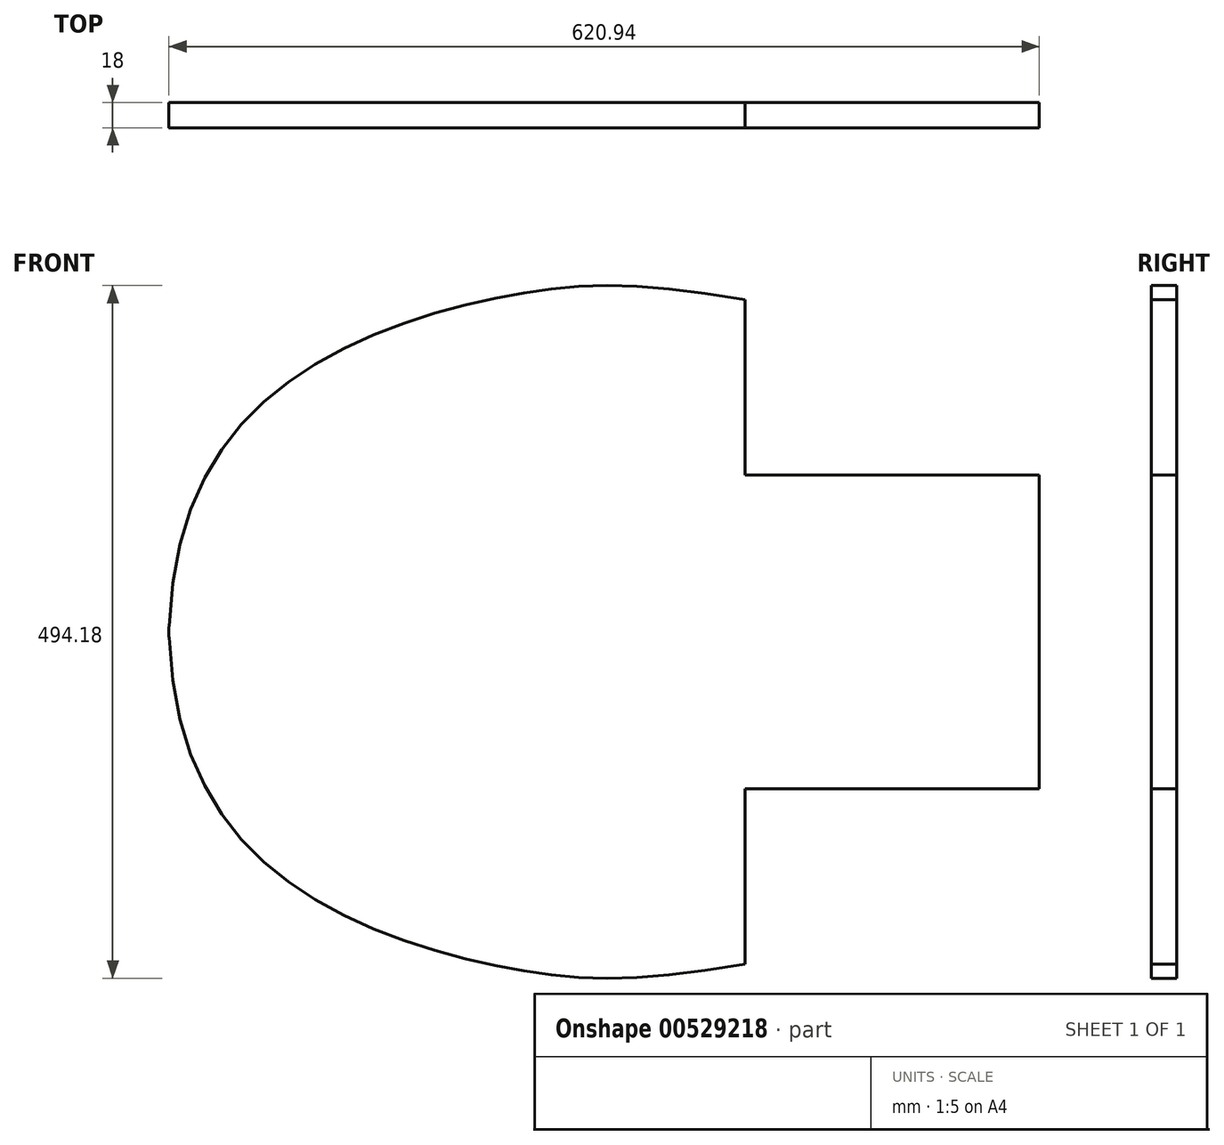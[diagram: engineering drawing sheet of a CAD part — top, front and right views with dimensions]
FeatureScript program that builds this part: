
annotation { "Feature Type Name" : "Feature", "Feature Type Description" : "" }
export const myFeature = defineFeature(function(context is Context, id is Id, definition is map)
    precondition{}
    {
        {
            var Q0;
            Q0=qCreatedBy(makeId("Front.planeOp"),FACE);
            var sketch = newSketch(context, id + "F0", { "sketchPlane" : qUnion([Q0])});
            skLineSegment(sketch, "E0", {"start": v(-355.6, 0) * mm, "end": v(355.6, 0) * mm, "construction": true});
            skLineSegment(sketch, "E1.0.1.0", {"start": v(-355.6, 50.8) * mm, "end": v(355.6, 50.8) * mm, "construction": true});
            skLineSegment(sketch, "E1.0.2.0", {"start": v(-355.6, 101.6) * mm, "end": v(355.6, 101.6) * mm, "construction": true});
            skLineSegment(sketch, "E1.0.3.0", {"start": v(-355.6, 152.4) * mm, "end": v(355.6, 152.4) * mm, "construction": true});
            skLineSegment(sketch, "E1.0.4.0", {"start": v(-355.6, 203.2) * mm, "end": v(355.6, 203.2) * mm, "construction": true});
            skLineSegment(sketch, "E1.0.5.0", {"start": v(-355.6, 254) * mm, "end": v(355.6, 254) * mm, "construction": true});
            skLineSegment(sketch, "E1.direction1", {"start": v(-355.6, 0) * mm, "end": v(-330.6, 0) * mm, "construction": true});
            skLineSegment(sketch, "E1.direction2", {"start": v(-355.6, 0) * mm, "end": v(-355.6, 50.8) * mm, "construction": true});
            skLineSegment(sketch, "E2.0.1.0", {"start": v(-355.6, -50.8) * mm, "end": v(355.6, -50.8) * mm, "construction": true});
            skLineSegment(sketch, "E2.0.2.0", {"start": v(-355.6, -101.6) * mm, "end": v(355.6, -101.6) * mm, "construction": true});
            skLineSegment(sketch, "E2.0.3.0", {"start": v(-355.6, -152.4) * mm, "end": v(355.6, -152.4) * mm, "construction": true});
            skLineSegment(sketch, "E2.0.4.0", {"start": v(-355.6, -203.2) * mm, "end": v(355.6, -203.2) * mm, "construction": true});
            skLineSegment(sketch, "E2.0.5.0", {"start": v(-355.6, -254) * mm, "end": v(355.6, -254) * mm, "construction": true});
            skLineSegment(sketch, "E2.direction1", {"start": v(-355.6, 0) * mm, "end": v(0, 0) * mm, "construction": true});
            skLineSegment(sketch, "E2.direction2", {"start": v(-355.6, 0) * mm, "end": v(-355.6, -50.8) * mm, "construction": true});
            skLineSegment(sketch, "E3", {"start": v(0, 254) * mm, "end": v(0, -254) * mm, "construction": true});
            skLineSegment(sketch, "E4.1.0.0", {"start": v(50.8, 254) * mm, "end": v(50.8, -254) * mm, "construction": true});
            skLineSegment(sketch, "E4.2.0.0", {"start": v(101.6, 254) * mm, "end": v(101.6, -254) * mm, "construction": true});
            skLineSegment(sketch, "E4.3.0.0", {"start": v(152.4, 254) * mm, "end": v(152.4, -254) * mm, "construction": true});
            skLineSegment(sketch, "E4.4.0.0", {"start": v(203.2, 254) * mm, "end": v(203.2, -254) * mm, "construction": true});
            skLineSegment(sketch, "E4.5.0.0", {"start": v(254, 254) * mm, "end": v(254, -254) * mm, "construction": true});
            skLineSegment(sketch, "E4.6.0.0", {"start": v(304.8, 254) * mm, "end": v(304.8, -254) * mm, "construction": true});
            skLineSegment(sketch, "E4.7.0.0", {"start": v(355.6, 254) * mm, "end": v(355.6, -254) * mm, "construction": true});
            skLineSegment(sketch, "E4.direction1", {"start": v(0, -254) * mm, "end": v(50.8, -254) * mm, "construction": true});
            skLineSegment(sketch, "E5.1.0.0", {"start": v(-50.8, 254) * mm, "end": v(-50.8, -254) * mm, "construction": true});
            skLineSegment(sketch, "E5.2.0.0", {"start": v(-101.6, 254) * mm, "end": v(-101.6, -254) * mm, "construction": true});
            skLineSegment(sketch, "E5.3.0.0", {"start": v(-152.4, 254) * mm, "end": v(-152.4, -254) * mm, "construction": true});
            skLineSegment(sketch, "E5.4.0.0", {"start": v(-203.2, 254) * mm, "end": v(-203.2, -254) * mm, "construction": true});
            skLineSegment(sketch, "E5.5.0.0", {"start": v(-254, 254) * mm, "end": v(-254, -254) * mm, "construction": true});
            skLineSegment(sketch, "E5.6.0.0", {"start": v(-304.8, 254) * mm, "end": v(-304.8, -254) * mm, "construction": true});
            skLineSegment(sketch, "E5.7.0.0", {"start": v(-355.6, 254) * mm, "end": v(-355.6, -254) * mm, "construction": true});
            skLineSegment(sketch, "E5.direction1", {"start": v(0, -254) * mm, "end": v(-50.8, -254) * mm, "construction": true});
            skLineSegment(sketch, "E6", {"start": v(-326, -217) * mm, "end": v(295, -217) * mm});
            skLineSegment(sketch, "E7", {"start": v(295, -217) * mm, "end": v(295, -105) * mm});
            skLineSegment(sketch, "E8", {"start": v(295, -105) * mm, "end": v(85, -105) * mm});
            skLineSegment(sketch, "E9", {"start": v(85, -105) * mm, "end": v(85, 20) * mm});
            skFitSpline(sketch, "E10", {"points": [v(85, 20) * mm, v(-82.23, 23.19) * mm, v(-240.84, -38.72) * mm, v(-326, -217) * mm], "startDerivative": vector(-701.8, 122.02) * mm, "endDerivative": vector(-22.07, -751.03) * mm});
            skFitSpline(sketch, "E11.MirrorCS", {"points": [v(85, -454) * mm, v(-82.23, -457.19) * mm, v(-240.84, -395.28) * mm, v(-326, -217) * mm], "startDerivative": vector(-701.8, -122.02) * mm, "endDerivative": vector(-22.07, 751.03) * mm});
            skLineSegment(sketch, "E12.MirrorCS", {"start": v(85, -329) * mm, "end": v(85, -454) * mm});
            skLineSegment(sketch, "E13.MirrorCS", {"start": v(295, -329) * mm, "end": v(85, -329) * mm});
            skLineSegment(sketch, "E14.MirrorCS", {"start": v(295, -217) * mm, "end": v(295, -329) * mm});
            skSolve(sketch);
        }
        {
            var Q0;
            Q0=makeQuery(id+"F0.imprint","IMPRINT",FACE,{"disambiguationData":[TD([[makeQuery(id+"F0.imprint","IMPRINT",EDGE,{"derivedFrom":sQuery(id+"F0.wireOp",EDGE,"E6")}),-1.0]])]});
            var Q1;
            Q1=makeQuery(id+"F0.imprint","IMPRINT",FACE,{"disambiguationData":[TD([[makeQuery(id+"F0.imprint","IMPRINT",EDGE,{"derivedFrom":sQuery(id+"F0.wireOp",EDGE,"E6")}),1.0]])]});
            extrude(context, id + "F1", {"entities" : qUnion([Q0, Q1]), "depth" : 18 * mm, "offsetDistance" : 25 * mm});
        }
        {
            var Q0;
            Q0=makeQuery(id+"F1.opExtrude","SWEPT_EDGE",EDGE,{"disambiguationData":[OSD([sQuery(id+"F0.wireOp",EDGE,"E6"),sQuery(id+"F0.wireOp",EDGE,"E10"),sQuery(id+"F0.wireOp",EDGE,"E11.MirrorCS")])]});
            fillet(context, id + "F2", {"entities" : qUnion([Q0]), "radius" : 100 * mm, "tangentPropagation" : true, "allowEdgeOverflow" : false});
        }
    });
